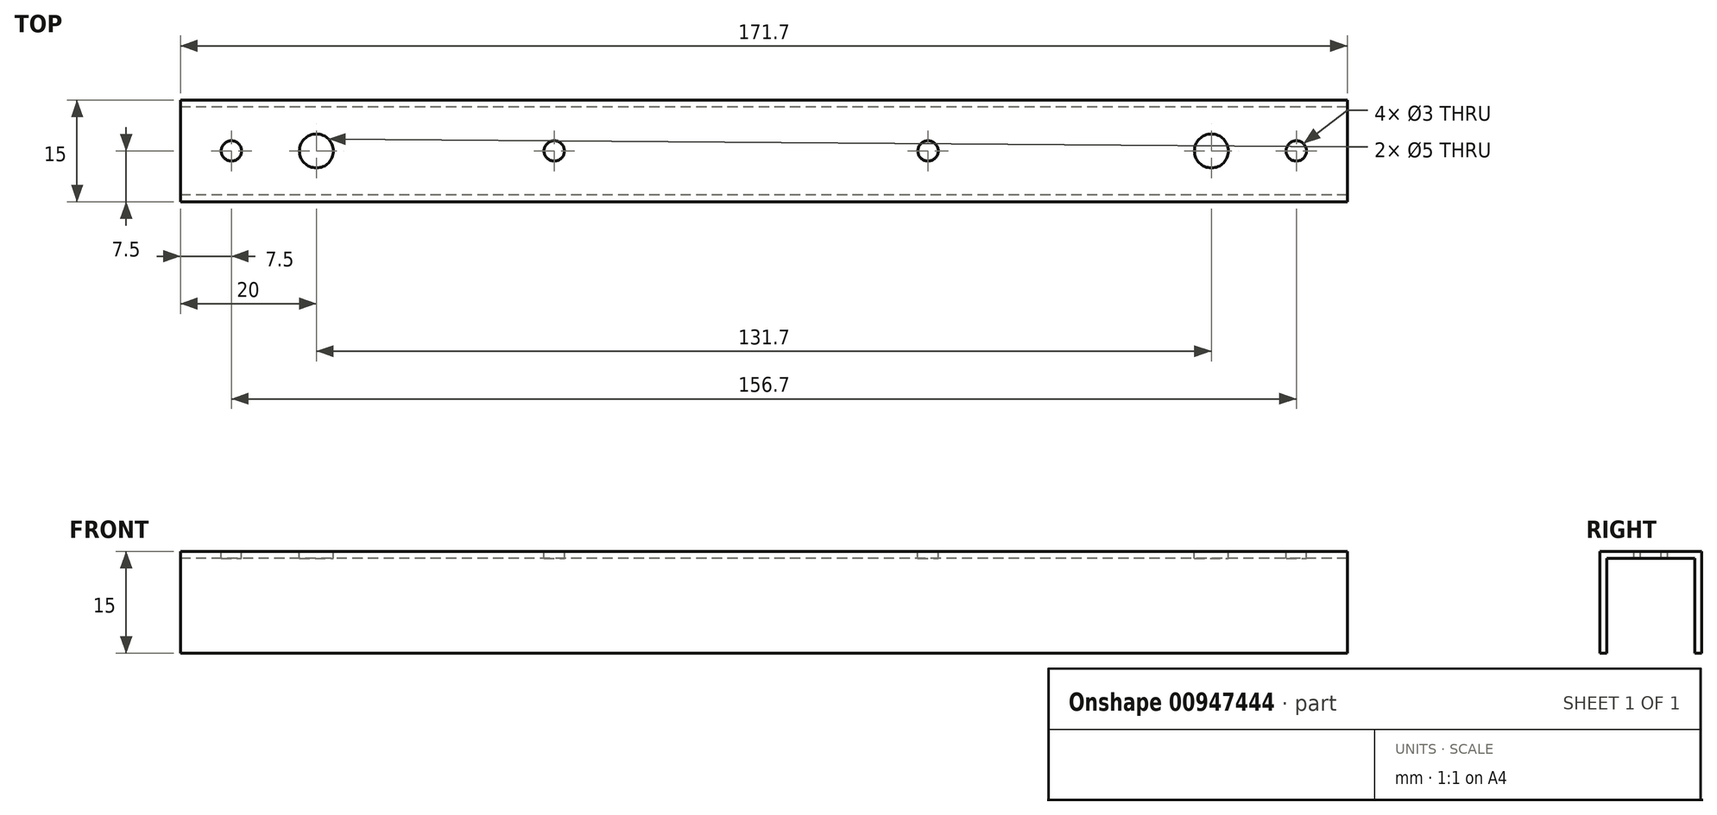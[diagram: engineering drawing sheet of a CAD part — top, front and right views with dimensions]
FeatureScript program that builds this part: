
annotation { "Feature Type Name" : "Feature", "Feature Type Description" : "" }
export const myFeature = defineFeature(function(context is Context, id is Id, definition is map)
    precondition{}
    {
        {
            var Q0;
            Q0=qCreatedBy(makeId("Right.planeOp"),FACE);
            var sketch = newSketch(context, id + "F0", { "sketchPlane" : qUnion([Q0])});
            skLineSegment(sketch, "E0.top", {"start": v(7.5, 7.5) * mm, "end": v(-7.5, 7.5) * mm});
            skLineSegment(sketch, "E0.left", {"start": v(7.5, -7.5) * mm, "end": v(7.5, 7.5) * mm});
            skLineSegment(sketch, "E0.right", {"start": v(-7.5, -7.5) * mm, "end": v(-7.5, 7.5) * mm});
            skPoint(sketch, "E0.middle", {"position": v(0, 0) * mm});
            skLineSegment(sketch, "E1.0", {"start": v(6.5, -7.5) * mm, "end": v(6.5, 6.5) * mm});
            skLineSegment(sketch, "E1.1", {"start": v(6.5, 6.5) * mm, "end": v(-6.5, 6.5) * mm});
            skLineSegment(sketch, "E1.2", {"start": v(-6.5, -7.5) * mm, "end": v(-6.5, 6.5) * mm});
            skLineSegment(sketch, "E2", {"start": v(-6.5, -7.5) * mm, "end": v(-7.5, -7.5) * mm});
            skLineSegment(sketch, "E3", {"start": v(6.5, -7.5) * mm, "end": v(7.5, -7.5) * mm});
            skSolve(sketch);
        }
        {
            var Q0;
            Q0=makeQuery(id+"F0.imprint","IMPRINT",FACE,{"disambiguationData":[TD([[makeQuery(id+"F0.imprint","IMPRINT",EDGE,{"derivedFrom":sQuery(id+"F0.wireOp",EDGE,"E0.top")}),1.0]])]});
            extrude(context, id + "F1", {"entities" : qUnion([Q0]), "depth" : (173.2 - 1.5) * mm, "offsetDistance" : 25 * mm});
        }
        {
            var Q0;
            Q0=makeQuery(id+"F1.opExtrude","SWEPT_FACE",FACE,{"disambiguationData":[OSD([sQuery(id+"F0.wireOp",EDGE,"E0.top")])]});
            var sketch = newSketch(context, id + "F2", { "sketchPlane" : qUnion([Q0])});
            skLineSegment(sketch, "E4", {"start": v(7.5, 7.5) * mm, "end": v(7.5, -7.5) * mm, "construction": true});
            skLineSegment(sketch, "E5", {"start": v(164.2, 7.5) * mm, "end": v(164.2, -7.5) * mm, "construction": true});
            skCircle(sketch, "E6", {"center": v(7.5, 0) * mm, "radius": 1.5 * mm});
            skCircle(sketch, "E7", {"center": v(164.2, 0) * mm, "radius": 1.5 * mm});
            skCircle(sketch, "E8", {"center": v(55, 0) * mm, "radius": 1.5 * mm});
            skCircle(sketch, "E9", {"center": v(110, 0) * mm, "radius": 1.5 * mm});
            skCircle(sketch, "E10", {"center": v(20, 0) * mm, "radius": 2.5 * mm});
            skCircle(sketch, "E11", {"center": v(151.7, 0) * mm, "radius": 2.5 * mm});
            skSolve(sketch);
        }
        {
            var Q0;
            Q0=makeQuery(id+"F2.imprint","IMPRINT",FACE,{"disambiguationData":[TD([[makeQuery(id+"F2.imprint","IMPRINT",EDGE,{"derivedFrom":sQuery(id+"F2.wireOp",EDGE,"E6")}),1.0]])]});
            var Q1;
            Q1=makeQuery(id+"F2.imprint","IMPRINT",FACE,{"disambiguationData":[TD([[makeQuery(id+"F2.imprint","IMPRINT",EDGE,{"derivedFrom":sQuery(id+"F2.wireOp",EDGE,"E8")}),1.0]])]});
            var Q2;
            Q2=makeQuery(id+"F2.imprint","IMPRINT",FACE,{"disambiguationData":[TD([[makeQuery(id+"F2.imprint","IMPRINT",EDGE,{"derivedFrom":sQuery(id+"F2.wireOp",EDGE,"E9")}),1.0]])]});
            var Q3;
            Q3=makeQuery(id+"F2.imprint","IMPRINT",FACE,{"disambiguationData":[TD([[makeQuery(id+"F2.imprint","IMPRINT",EDGE,{"derivedFrom":sQuery(id+"F2.wireOp",EDGE,"E7")}),1.0]])]});
            var Q4;
            Q4=makeQuery(id+"F2.imprint","IMPRINT",FACE,{"disambiguationData":[TD([[makeQuery(id+"F2.imprint","IMPRINT",EDGE,{"derivedFrom":sQuery(id+"F2.wireOp",EDGE,"E10")}),1.0]])]});
            var Q5;
            Q5=makeQuery(id+"F2.imprint","IMPRINT",FACE,{"disambiguationData":[TD([[makeQuery(id+"F2.imprint","IMPRINT",EDGE,{"derivedFrom":sQuery(id+"F2.wireOp",EDGE,"E11")}),1.0]])]});
            extrude(context, id + "F3", {"entities" : qUnion([Q0, Q1, Q2, Q3, Q4, Q5]), "operationType" : NewBodyOperationType.REMOVE, "endBound" : BoundingType.UP_TO_NEXT, "oppositeDirection" : true, "depth" : 25 * mm, "offsetDistance" : 25 * mm});
        }
    });
